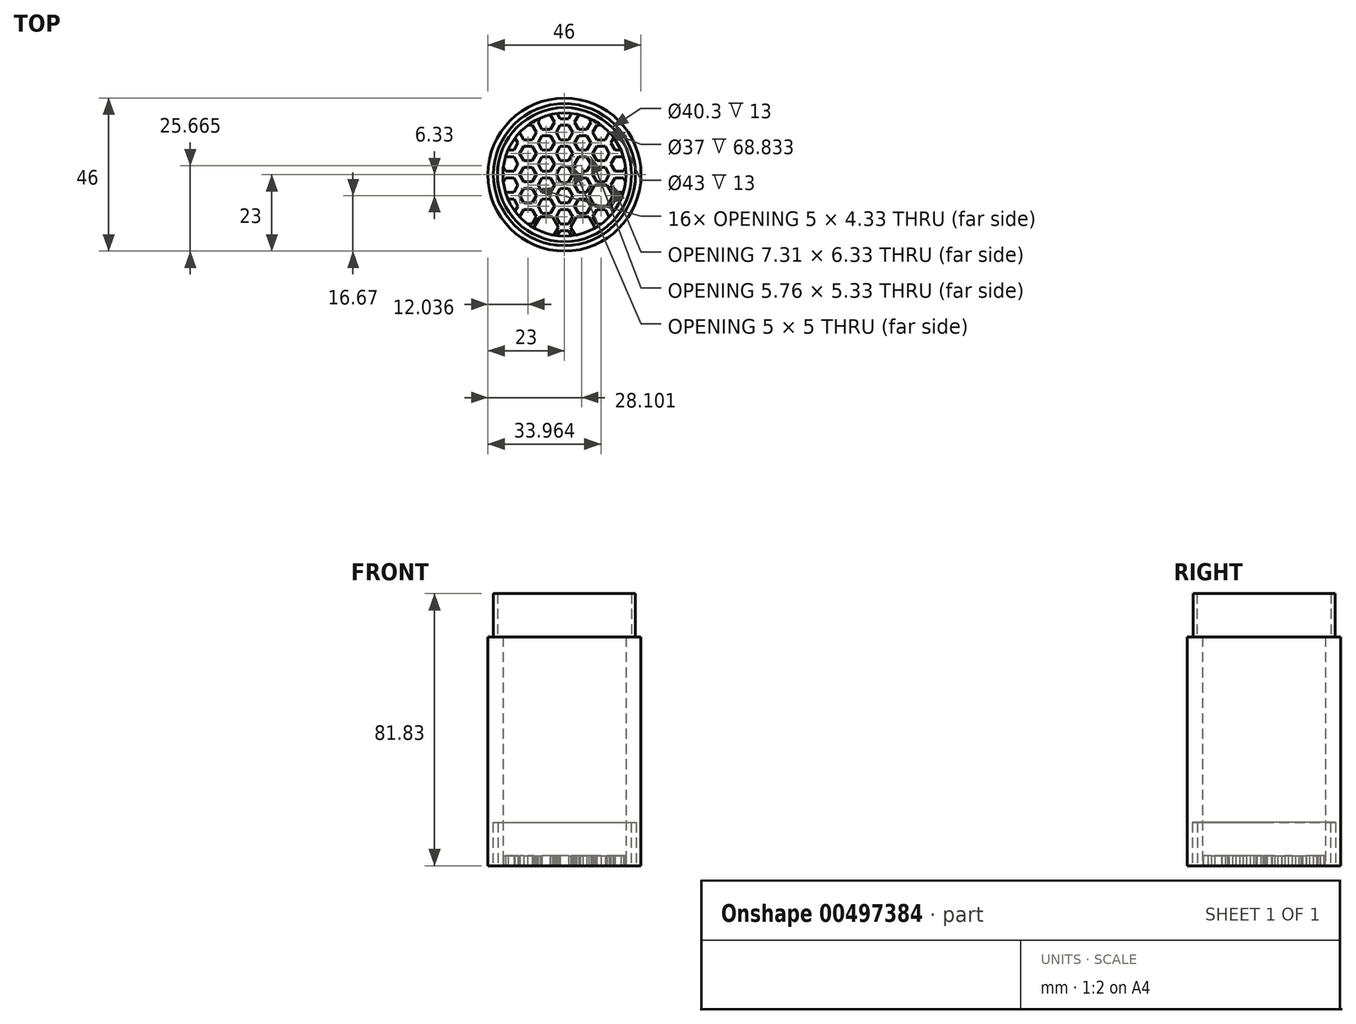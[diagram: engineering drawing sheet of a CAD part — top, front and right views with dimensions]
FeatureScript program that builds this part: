
annotation { "Feature Type Name" : "Feature", "Feature Type Description" : "" }
export const myFeature = defineFeature(function(context is Context, id is Id, definition is map)
    precondition{}
    {
        {
            var Q0;
            Q0=qCreatedBy(makeId("Front.planeOp"),FACE);
            var sketch = newSketch(context, id + "F0", { "sketchPlane" : qUnion([Q0])});
            skLineSegment(sketch, "E0", {"start": v(0, 0) * mm, "end": v(20, 0) * mm});
            skLineSegment(sketch, "E1.bottom", {"start": v(20, 0) * mm, "end": v(18.5, 0) * mm});
            skLineSegment(sketch, "E1.top", {"start": v(20, -13) * mm, "end": v(18.5, -13) * mm});
            skLineSegment(sketch, "E1.left", {"start": v(20, 0) * mm, "end": v(20, -13) * mm});
            skLineSegment(sketch, "E1.right", {"start": v(18.5, 0) * mm, "end": v(18.5, -13) * mm});
            skLineSegment(sketch, "E2.bottom", {"start": v(21.5, 0) * mm, "end": v(20, 0) * mm});
            skLineSegment(sketch, "E2.top", {"start": v(21.5, -13) * mm, "end": v(20, -13) * mm});
            skLineSegment(sketch, "E2.left", {"start": v(21.5, 0) * mm, "end": v(21.5, -13) * mm});
            skLineSegment(sketch, "E3.bottom", {"start": v(23, 0) * mm, "end": v(21.5, 0) * mm});
            skLineSegment(sketch, "E3.top", {"start": v(23, -13) * mm, "end": v(21.5, -13) * mm});
            skLineSegment(sketch, "E3.left", {"start": v(23, 0) * mm, "end": v(23, -13) * mm});
            skLineSegment(sketch, "E4.bottom", {"start": v(23, 0) * mm, "end": v(0, 0) * mm});
            skLineSegment(sketch, "E4.top", {"start": v(23, 55.83) * mm, "end": v(0, 55.83) * mm});
            skLineSegment(sketch, "E4.left", {"start": v(23, 0) * mm, "end": v(23, 55.83) * mm});
            skLineSegment(sketch, "E4.right", {"start": v(0, 0) * mm, "end": v(0, 55.83) * mm});
            skLineSegment(sketch, "E5.bottom", {"start": v(23, 55.83) * mm, "end": v(21.35, 55.83) * mm});
            skLineSegment(sketch, "E5.top", {"start": v(23, 68.83) * mm, "end": v(21.35, 68.83) * mm});
            skLineSegment(sketch, "E5.left", {"start": v(23, 55.83) * mm, "end": v(23, 68.83) * mm});
            skLineSegment(sketch, "E5.right", {"start": v(21.35, 55.83) * mm, "end": v(21.35, 68.83) * mm});
            skLineSegment(sketch, "E6.bottom", {"start": v(21.35, 68.83) * mm, "end": v(20.15, 68.83) * mm});
            skLineSegment(sketch, "E6.top", {"start": v(21.35, 55.83) * mm, "end": v(20.15, 55.83) * mm});
            skLineSegment(sketch, "E6.left", {"start": v(21.35, 68.83) * mm, "end": v(21.35, 55.83) * mm});
            skLineSegment(sketch, "E6.right", {"start": v(20.15, 68.83) * mm, "end": v(20.15, 55.83) * mm});
            skLineSegment(sketch, "E7.bottom", {"start": v(20.15, 68.83) * mm, "end": v(18.5, 68.83) * mm});
            skLineSegment(sketch, "E7.top", {"start": v(20.15, 55.83) * mm, "end": v(18.5, 55.83) * mm});
            skLineSegment(sketch, "E7.right", {"start": v(18.5, 68.83) * mm, "end": v(18.5, 55.83) * mm});
            skLineSegment(sketch, "E8", {"start": v(18.5, 55.83) * mm, "end": v(18.5, 0) * mm});
            skSolve(sketch);
        }
        {
            var Q0;
            {var subQ2=sQuery(id+"F0.wireOp",EDGE,"E5.right");Q0=makeQuery(id+"F0.imprint","IMPRINT",FACE,{"disambiguationData":[TD([[makeQuery(id+"F0.imprint","IMPRINT",EDGE,{"derivedFrom":subQ2}),1.0]])]});}
            var Q1;
            Q1=makeQuery(id+"F0.imprint","IMPRINT",FACE,{"disambiguationData":[TD([[makeQuery(id+"F0.imprint","IMPRINT",EDGE,{"derivedFrom":sQuery(id+"F0.wireOp",EDGE,"E2.left")}),1.0]])]});
            var Q2;
            Q2=makeQuery(id+"F0.imprint","IMPRINT",FACE,{"disambiguationData":[TD([[makeQuery(id+"F0.imprint","IMPRINT",EDGE,{"derivedFrom":sQuery(id+"F0.wireOp",EDGE,"E1.top")}),-1.0]])]});
            var Q3;
            {var subQ3=sQuery(id+"F0.wireOp",EDGE,"E2.bottom");Q3=makeQuery(id+"F0.imprint","IMPRINT",FACE,{"disambiguationData":[TD([[makeQuery(id+"F0.imprint","IMPRINT",EDGE,{"derivedFrom":subQ3}),-1.0]])]});}
            var Q4;
            Q4=sQuery(id+"F0.wireOp",EDGE,"E4.right");
            revolve(context, id + "F1", {"entities" : qUnion([Q0, Q1, Q2, Q3]), "axis" : qUnion([Q4]), "revolveType" : RevolveType.FULL});
        }
        {
            var Q0;
            Q0=makeQuery(id+"F1.opRevolve","SWEPT_FACE",FACE,{"disambiguationData":[OSD([sQuery(id+"F0.wireOp",EDGE,"E1.top")])]});
            var sketch = newSketch(context, id + "F2", { "sketchPlane" : qUnion([Q0])});
            skCircle(sketch, "E9.0", {"center": v(0, 0) * mm, "radius": 20 * mm});
            skCircle(sketch, "E10.0", {"center": v(0, 0) * mm, "radius": 18.5 * mm});
            skCircle(sketch, "E11", {"center": v(0, 0) * mm, "radius": 2.5 * mm});
            skLineSegment(sketch, "E12", {"start": v(-2.5, 0) * mm, "end": v(2.5, 0) * mm});
            skLineSegment(sketch, "E13", {"start": v(0, 2.5) * mm, "end": v(0, -2.5) * mm});
            skArc(sketch, "E14", {"start": v(0, 0) * mm, "mid": v(4.67, 1.25) * mm, "end": v(1.25, -2.17) * mm});
            skArc(sketch, "E15", {"start": v(0, 0) * mm, "mid": v(-4.67, 1.25) * mm, "end": v(-1.25, -2.17) * mm});
            skPoint(sketch, "E16", {"position": v(1.25, -2.17) * mm});
            skPoint(sketch, "E17", {"position": v(1.25, 2.17) * mm});
            skPoint(sketch, "E18", {"position": v(-1.25, 2.17) * mm});
            skPoint(sketch, "E19", {"position": v(-1.25, -2.17) * mm});
            skLineSegment(sketch, "E20", {"start": v(1.25, -2.17) * mm, "end": v(2.5, 0) * mm});
            skLineSegment(sketch, "E21", {"start": v(1.25, 2.17) * mm, "end": v(2.5, 0) * mm});
            skLineSegment(sketch, "E22", {"start": v(1.25, 2.17) * mm, "end": v(-1.25, 2.17) * mm});
            skLineSegment(sketch, "E23", {"start": v(-1.25, 2.17) * mm, "end": v(-2.5, 0) * mm});
            skLineSegment(sketch, "E24", {"start": v(-2.5, 0) * mm, "end": v(-1.25, -2.17) * mm});
            skLineSegment(sketch, "E25", {"start": v(-1.25, -2.17) * mm, "end": v(1.25, -2.17) * mm});
            skLineSegment(sketch, "E26.0", {"start": v(-3.65, 0) * mm, "end": v(-1.83, -3.17) * mm});
            skLineSegment(sketch, "E26.1", {"start": v(1.83, -3.17) * mm, "end": v(3.65, 0) * mm});
            skLineSegment(sketch, "E26.2", {"start": v(1.83, 3.17) * mm, "end": v(3.65, 0) * mm});
            skLineSegment(sketch, "E26.3", {"start": v(-1.83, -3.17) * mm, "end": v(1.83, -3.17) * mm});
            skLineSegment(sketch, "E26.4", {"start": v(1.83, 3.17) * mm, "end": v(-1.83, 3.17) * mm});
            skLineSegment(sketch, "E26.5", {"start": v(-1.83, 3.17) * mm, "end": v(-3.65, 0) * mm});
            skLineSegment(sketch, "E27.MirrorCS", {"start": v(-4.23, -1) * mm, "end": v(-2.98, -3.17) * mm});
            skLineSegment(sketch, "E28.MirrorCS", {"start": v(-2.98, -3.17) * mm, "end": v(-4.23, -5.33) * mm});
            skLineSegment(sketch, "E29.MirrorCS", {"start": v(-4.23, -5.33) * mm, "end": v(-6.73, -5.33) * mm});
            skLineSegment(sketch, "E30.MirrorCS", {"start": v(-6.73, -1) * mm, "end": v(-4.23, -1) * mm});
            skLineSegment(sketch, "E31.MirrorCS", {"start": v(-7.98, -3.17) * mm, "end": v(-6.73, -1) * mm});
            skLineSegment(sketch, "E32.MirrorCS", {"start": v(-7.98, -3.17) * mm, "end": v(-6.73, -5.33) * mm});
            skLineSegment(sketch, "E33.MirrorCS", {"start": v(-1.83, -3.17) * mm, "end": v(-3.65, -6.33) * mm});
            skLineSegment(sketch, "E34.MirrorCS", {"start": v(-7.3, 0) * mm, "end": v(-3.65, 0) * mm});
            skLineSegment(sketch, "E35.MirrorCS", {"start": v(-9.14, -3.17) * mm, "end": v(-7.3, 0) * mm});
            skLineSegment(sketch, "E36.MirrorCS", {"start": v(-3.65, -6.33) * mm, "end": v(-7.3, -6.33) * mm});
            skLineSegment(sketch, "E37.MirrorCS", {"start": v(-9.14, -3.17) * mm, "end": v(-7.3, -6.33) * mm});
            skLineSegment(sketch, "E38.MirrorCS", {"start": v(-7.3, 6.33) * mm, "end": v(-3.65, 6.33) * mm});
            skLineSegment(sketch, "E39.MirrorCS", {"start": v(-9.14, 9.5) * mm, "end": v(-7.3, 6.33) * mm});
            skLineSegment(sketch, "E40.MirrorCS", {"start": v(-7.98, 9.5) * mm, "end": v(-6.73, 7.33) * mm});
            skLineSegment(sketch, "E41.MirrorCS", {"start": v(-6.73, 7.33) * mm, "end": v(-4.23, 7.33) * mm});
            skLineSegment(sketch, "E42.MirrorCS", {"start": v(-3.65, 12.66) * mm, "end": v(-7.3, 12.66) * mm});
            skLineSegment(sketch, "E43.MirrorCS", {"start": v(-4.23, 11.66) * mm, "end": v(-6.73, 11.66) * mm});
            skLineSegment(sketch, "E44.MirrorCS", {"start": v(-7.98, 9.5) * mm, "end": v(-6.73, 11.66) * mm});
            skLineSegment(sketch, "E45.MirrorCS", {"start": v(-9.14, 9.5) * mm, "end": v(-7.3, 12.66) * mm});
            skLineSegment(sketch, "E46.MirrorCS", {"start": v(-2.98, 9.5) * mm, "end": v(-4.23, 11.66) * mm});
            skLineSegment(sketch, "E47.MirrorCS", {"start": v(-1.83, 9.5) * mm, "end": v(-3.65, 12.66) * mm});
            skLineSegment(sketch, "E48.MirrorCS", {"start": v(-4.23, 7.33) * mm, "end": v(-2.98, 9.5) * mm});
            skLineSegment(sketch, "E49.MirrorCS", {"start": v(-3.65, 6.33) * mm, "end": v(-1.83, 9.5) * mm});
            skLineSegment(sketch, "E50.MirrorCS", {"start": v(1.25, 4.17) * mm, "end": v(-1.25, 4.17) * mm});
            skLineSegment(sketch, "E51.MirrorCS", {"start": v(-1.25, 4.17) * mm, "end": v(-2.5, 6.33) * mm});
            skLineSegment(sketch, "E52.MirrorCS", {"start": v(-1.83, 3.17) * mm, "end": v(-3.65, 6.33) * mm});
            skLineSegment(sketch, "E53.MirrorCS", {"start": v(1.83, 3.17) * mm, "end": v(3.65, 6.33) * mm});
            skLineSegment(sketch, "E54.MirrorCS", {"start": v(1.25, 4.17) * mm, "end": v(2.5, 6.33) * mm});
            skLineSegment(sketch, "E55.MirrorCS", {"start": v(1.25, 8.5) * mm, "end": v(2.5, 6.33) * mm});
            skLineSegment(sketch, "E56.MirrorCS", {"start": v(1.83, 9.5) * mm, "end": v(3.65, 6.33) * mm});
            skLineSegment(sketch, "E57.MirrorCS", {"start": v(-1.83, 9.5) * mm, "end": v(1.83, 9.5) * mm});
            skLineSegment(sketch, "E58.MirrorCS", {"start": v(-1.25, 8.5) * mm, "end": v(1.25, 8.5) * mm});
            skLineSegment(sketch, "E59.MirrorCS", {"start": v(-2.5, 6.33) * mm, "end": v(-1.25, 8.5) * mm});
            skLineSegment(sketch, "E60.MirrorCS", {"start": v(-6.73, 1) * mm, "end": v(-4.23, 1) * mm});
            skLineSegment(sketch, "E61.MirrorCS", {"start": v(-7.98, 3.17) * mm, "end": v(-6.73, 1) * mm});
            skLineSegment(sketch, "E62.MirrorCS", {"start": v(-9.14, 3.17) * mm, "end": v(-7.3, 0) * mm});
            skLineSegment(sketch, "E63.MirrorCS", {"start": v(-9.14, 3.17) * mm, "end": v(-7.3, 6.33) * mm});
            skLineSegment(sketch, "E64.MirrorCS", {"start": v(-7.98, 3.17) * mm, "end": v(-6.73, 5.33) * mm});
            skLineSegment(sketch, "E65.MirrorCS", {"start": v(-3.65, 6.33) * mm, "end": v(-7.3, 6.33) * mm});
            skLineSegment(sketch, "E66.MirrorCS", {"start": v(-4.23, 5.33) * mm, "end": v(-6.73, 5.33) * mm});
            skLineSegment(sketch, "E67.MirrorCS", {"start": v(-2.98, 3.17) * mm, "end": v(-4.23, 5.33) * mm});
            skLineSegment(sketch, "E68.MirrorCS", {"start": v(-4.23, 1) * mm, "end": v(-2.98, 3.17) * mm});
            skLineSegment(sketch, "E69.MirrorCS", {"start": v(-1.25, -4.17) * mm, "end": v(1.25, -4.17) * mm});
            skLineSegment(sketch, "E70.MirrorCS", {"start": v(-2.5, -6.33) * mm, "end": v(-1.25, -4.17) * mm});
            skLineSegment(sketch, "E71.MirrorCS", {"start": v(-1.25, -8.5) * mm, "end": v(-2.5, -6.33) * mm});
            skLineSegment(sketch, "E72.MirrorCS", {"start": v(1.25, -8.5) * mm, "end": v(-1.25, -8.5) * mm});
            skLineSegment(sketch, "E73.MirrorCS", {"start": v(1.25, -8.5) * mm, "end": v(2.5, -6.33) * mm});
            skLineSegment(sketch, "E74.MirrorCS", {"start": v(1.25, -4.17) * mm, "end": v(2.5, -6.33) * mm});
            skLineSegment(sketch, "E75.MirrorCS", {"start": v(1.83, -3.17) * mm, "end": v(3.65, -6.33) * mm});
            skLineSegment(sketch, "E76.MirrorCS", {"start": v(1.83, -9.5) * mm, "end": v(3.65, -6.33) * mm});
            skLineSegment(sketch, "E77.MirrorCS", {"start": v(1.83, -9.5) * mm, "end": v(-1.83, -9.5) * mm});
            skLineSegment(sketch, "E78.MirrorCS", {"start": v(-1.83, -9.5) * mm, "end": v(-3.65, -6.33) * mm});
            skLineSegment(sketch, "E79.MirrorCS", {"start": v(-4.23, -7.33) * mm, "end": v(-2.98, -9.5) * mm});
            skLineSegment(sketch, "E80.MirrorCS", {"start": v(-6.73, -7.33) * mm, "end": v(-4.23, -7.33) * mm});
            skLineSegment(sketch, "E81.MirrorCS", {"start": v(-7.98, -9.5) * mm, "end": v(-6.73, -7.33) * mm});
            skLineSegment(sketch, "E82.MirrorCS", {"start": v(-7.98, -9.5) * mm, "end": v(-6.73, -11.66) * mm});
            skLineSegment(sketch, "E83.MirrorCS", {"start": v(-4.23, -11.66) * mm, "end": v(-6.73, -11.66) * mm});
            skLineSegment(sketch, "E84.MirrorCS", {"start": v(-2.98, -9.5) * mm, "end": v(-4.23, -11.66) * mm});
            skLineSegment(sketch, "E85.MirrorCS", {"start": v(-9.14, -9.5) * mm, "end": v(-7.3, -6.33) * mm});
            skLineSegment(sketch, "E86.MirrorCS", {"start": v(-9.14, -9.5) * mm, "end": v(-7.3, -12.66) * mm});
            skLineSegment(sketch, "E87.MirrorCS", {"start": v(-7.3, -12.66) * mm, "end": v(-3.65, -12.66) * mm});
            skLineSegment(sketch, "E88.MirrorCS", {"start": v(-1.83, -9.5) * mm, "end": v(-3.65, -12.66) * mm});
            skLineSegment(sketch, "E89.MirrorCS", {"start": v(1.83, -9.5) * mm, "end": v(3.65, -12.66) * mm});
            skLineSegment(sketch, "E90.MirrorCS", {"start": v(7.3, -12.66) * mm, "end": v(3.65, -12.66) * mm});
            skLineSegment(sketch, "E91.MirrorCS", {"start": v(9.14, -9.5) * mm, "end": v(7.3, -12.66) * mm});
            skLineSegment(sketch, "E92.MirrorCS", {"start": v(9.14, -9.5) * mm, "end": v(7.3, -6.33) * mm});
            skLineSegment(sketch, "E93.MirrorCS", {"start": v(3.65, -6.33) * mm, "end": v(7.3, -6.33) * mm});
            skLineSegment(sketch, "E94.MirrorCS", {"start": v(9.14, -3.17) * mm, "end": v(7.3, -6.33) * mm});
            skLineSegment(sketch, "E95.MirrorCS", {"start": v(9.14, -3.17) * mm, "end": v(7.3, 0) * mm});
            skLineSegment(sketch, "E96.MirrorCS", {"start": v(7.3, 0) * mm, "end": v(3.65, 0) * mm});
            skLineSegment(sketch, "E97.MirrorCS", {"start": v(9.14, 3.17) * mm, "end": v(7.3, 0) * mm});
            skLineSegment(sketch, "E98.MirrorCS", {"start": v(9.14, 3.17) * mm, "end": v(7.3, 6.33) * mm});
            skLineSegment(sketch, "E99.MirrorCS", {"start": v(7.3, 6.33) * mm, "end": v(3.65, 6.33) * mm});
            skLineSegment(sketch, "E100.MirrorCS", {"start": v(7.98, 9.5) * mm, "end": v(6.73, 7.33) * mm});
            skLineSegment(sketch, "E101.MirrorCS", {"start": v(9.14, 9.5) * mm, "end": v(7.3, 12.66) * mm});
            skLineSegment(sketch, "E102.MirrorCS", {"start": v(3.65, 12.66) * mm, "end": v(7.3, 12.66) * mm});
            skLineSegment(sketch, "E103.MirrorCS", {"start": v(1.83, 9.5) * mm, "end": v(3.65, 12.66) * mm});
            skLineSegment(sketch, "E104.MirrorCS", {"start": v(9.14, 9.5) * mm, "end": v(7.3, 6.33) * mm});
            skLineSegment(sketch, "E105.MirrorCS", {"start": v(7.98, 9.5) * mm, "end": v(6.73, 11.66) * mm});
            skLineSegment(sketch, "E106.MirrorCS", {"start": v(4.23, 11.66) * mm, "end": v(6.73, 11.66) * mm});
            skLineSegment(sketch, "E107.MirrorCS", {"start": v(2.98, 9.5) * mm, "end": v(4.23, 11.66) * mm});
            skLineSegment(sketch, "E108.MirrorCS", {"start": v(4.23, 7.33) * mm, "end": v(2.98, 9.5) * mm});
            skLineSegment(sketch, "E109.MirrorCS", {"start": v(6.73, 7.33) * mm, "end": v(4.23, 7.33) * mm});
            skLineSegment(sketch, "E110.MirrorCS", {"start": v(4.23, 5.33) * mm, "end": v(6.73, 5.33) * mm});
            skLineSegment(sketch, "E111.MirrorCS", {"start": v(7.98, 3.17) * mm, "end": v(6.73, 5.33) * mm});
            skLineSegment(sketch, "E112.MirrorCS", {"start": v(2.98, 3.17) * mm, "end": v(4.23, 5.33) * mm});
            skLineSegment(sketch, "E113.MirrorCS", {"start": v(7.98, 3.17) * mm, "end": v(6.73, 1) * mm});
            skLineSegment(sketch, "E114.MirrorCS", {"start": v(6.73, 1) * mm, "end": v(4.23, 1) * mm});
            skLineSegment(sketch, "E115.MirrorCS", {"start": v(4.23, 1) * mm, "end": v(2.98, 3.17) * mm});
            skLineSegment(sketch, "E116.MirrorCS", {"start": v(2.98, -3.17) * mm, "end": v(4.23, -5.33) * mm});
            skLineSegment(sketch, "E117.MirrorCS", {"start": v(4.23, -5.33) * mm, "end": v(6.73, -5.33) * mm});
            skLineSegment(sketch, "E118.MirrorCS", {"start": v(7.98, -3.17) * mm, "end": v(6.73, -5.33) * mm});
            skLineSegment(sketch, "E119.MirrorCS", {"start": v(7.98, -3.17) * mm, "end": v(6.73, -1) * mm});
            skLineSegment(sketch, "E120.MirrorCS", {"start": v(6.73, -1) * mm, "end": v(4.23, -1) * mm});
            skLineSegment(sketch, "E121.MirrorCS", {"start": v(4.23, -1) * mm, "end": v(2.98, -3.17) * mm});
            skLineSegment(sketch, "E122.MirrorCS", {"start": v(4.23, -7.33) * mm, "end": v(2.98, -9.5) * mm});
            skLineSegment(sketch, "E123.MirrorCS", {"start": v(6.73, -7.33) * mm, "end": v(4.23, -7.33) * mm});
            skLineSegment(sketch, "E124.MirrorCS", {"start": v(7.98, -9.5) * mm, "end": v(6.73, -7.33) * mm});
            skLineSegment(sketch, "E125.MirrorCS", {"start": v(7.98, -9.5) * mm, "end": v(6.73, -11.66) * mm});
            skLineSegment(sketch, "E126.MirrorCS", {"start": v(4.23, -11.66) * mm, "end": v(6.73, -11.66) * mm});
            skLineSegment(sketch, "E127.MirrorCS", {"start": v(2.98, -9.5) * mm, "end": v(4.23, -11.66) * mm});
            skLineSegment(sketch, "E128", {"start": v(5.48, 1) * mm, "end": v(5.48, -1) * mm});
            skLineSegment(sketch, "E129.MirrorCS", {"start": v(12.8, 9.5) * mm, "end": v(9.14, 9.5) * mm});
            skLineSegment(sketch, "E130.MirrorCS", {"start": v(9.14, 3.17) * mm, "end": v(12.8, 3.17) * mm});
            skLineSegment(sketch, "E131.MirrorCS", {"start": v(12.8, -3.17) * mm, "end": v(9.14, -3.17) * mm});
            skLineSegment(sketch, "E132.MirrorCS", {"start": v(9.14, -9.5) * mm, "end": v(12.8, -9.5) * mm});
            skLineSegment(sketch, "E133.MirrorCS", {"start": v(14.62, 0) * mm, "end": v(12.8, -3.17) * mm});
            skLineSegment(sketch, "E134.MirrorCS", {"start": v(12.8, 3.17) * mm, "end": v(14.62, 0) * mm});
            skLineSegment(sketch, "E135.MirrorCS", {"start": v(12.8, 3.17) * mm, "end": v(14.62, 6.33) * mm});
            skLineSegment(sketch, "E136.MirrorCS", {"start": v(14.62, 6.33) * mm, "end": v(12.8, 9.5) * mm});
            skLineSegment(sketch, "E137.MirrorCS", {"start": v(12.8, -3.17) * mm, "end": v(14.62, -6.33) * mm});
            skLineSegment(sketch, "E138.MirrorCS", {"start": v(12.8, -9.5) * mm, "end": v(14.62, -6.33) * mm});
            skLineSegment(sketch, "E139.MirrorCS", {"start": v(9.71, -4.17) * mm, "end": v(8.46, -6.33) * mm});
            skLineSegment(sketch, "E140.MirrorCS", {"start": v(9.71, -8.5) * mm, "end": v(8.46, -6.33) * mm});
            skLineSegment(sketch, "E141.MirrorCS", {"start": v(9.71, -8.5) * mm, "end": v(12.21, -8.5) * mm});
            skLineSegment(sketch, "E142.MirrorCS", {"start": v(12.21, -8.5) * mm, "end": v(13.46, -6.33) * mm});
            skLineSegment(sketch, "E143.MirrorCS", {"start": v(13.46, -6.33) * mm, "end": v(12.21, -4.17) * mm});
            skLineSegment(sketch, "E144.MirrorCS", {"start": v(12.21, -4.17) * mm, "end": v(9.71, -4.17) * mm});
            skLineSegment(sketch, "E145.MirrorCS", {"start": v(9.71, 4.17) * mm, "end": v(12.21, 4.17) * mm});
            skLineSegment(sketch, "E146.MirrorCS", {"start": v(9.71, 4.17) * mm, "end": v(8.46, 6.33) * mm});
            skLineSegment(sketch, "E147.MirrorCS", {"start": v(9.71, 8.5) * mm, "end": v(8.46, 6.33) * mm});
            skLineSegment(sketch, "E148.MirrorCS", {"start": v(12.21, 8.5) * mm, "end": v(9.71, 8.5) * mm});
            skLineSegment(sketch, "E149.MirrorCS", {"start": v(12.21, 4.17) * mm, "end": v(13.46, 6.33) * mm});
            skLineSegment(sketch, "E150.MirrorCS", {"start": v(13.46, 6.33) * mm, "end": v(12.21, 8.5) * mm});
            skLineSegment(sketch, "E151.MirrorCS", {"start": v(9.71, 2.17) * mm, "end": v(12.21, 2.17) * mm});
            skLineSegment(sketch, "E152.MirrorCS", {"start": v(12.21, 2.17) * mm, "end": v(13.46, 0) * mm});
            skLineSegment(sketch, "E153.MirrorCS", {"start": v(13.46, 0) * mm, "end": v(12.21, -2.17) * mm});
            skLineSegment(sketch, "E154.MirrorCS", {"start": v(12.21, -2.17) * mm, "end": v(9.71, -2.17) * mm});
            skLineSegment(sketch, "E155.MirrorCS", {"start": v(9.71, -2.17) * mm, "end": v(8.46, 0) * mm});
            skLineSegment(sketch, "E156.MirrorCS", {"start": v(9.71, 2.17) * mm, "end": v(8.46, 0) * mm});
            skLineSegment(sketch, "E157.MirrorCS", {"start": v(-9.14, -9.5) * mm, "end": v(-12.8, -9.5) * mm});
            skLineSegment(sketch, "E158.MirrorCS", {"start": v(-12.8, -9.5) * mm, "end": v(-14.62, -6.33) * mm});
            skLineSegment(sketch, "E159.MirrorCS", {"start": v(-12.8, -3.17) * mm, "end": v(-14.62, -6.33) * mm});
            skLineSegment(sketch, "E160.MirrorCS", {"start": v(-12.8, -3.17) * mm, "end": v(-9.14, -3.17) * mm});
            skLineSegment(sketch, "E161.MirrorCS", {"start": v(-14.62, 0) * mm, "end": v(-12.8, -3.17) * mm});
            skLineSegment(sketch, "E162.MirrorCS", {"start": v(-12.8, 3.17) * mm, "end": v(-14.62, 0) * mm});
            skLineSegment(sketch, "E163.MirrorCS", {"start": v(-9.14, 3.17) * mm, "end": v(-12.8, 3.17) * mm});
            skLineSegment(sketch, "E164.MirrorCS", {"start": v(-12.8, 3.17) * mm, "end": v(-14.62, 6.33) * mm});
            skLineSegment(sketch, "E165.MirrorCS", {"start": v(-14.62, 6.33) * mm, "end": v(-12.8, 9.5) * mm});
            skLineSegment(sketch, "E166.MirrorCS", {"start": v(-12.8, 9.5) * mm, "end": v(-9.14, 9.5) * mm});
            skLineSegment(sketch, "E167.MirrorCS", {"start": v(-12.21, 8.5) * mm, "end": v(-9.71, 8.5) * mm});
            skLineSegment(sketch, "E168.MirrorCS", {"start": v(-13.46, 6.33) * mm, "end": v(-12.21, 8.5) * mm});
            skLineSegment(sketch, "E169.MirrorCS", {"start": v(-9.71, 8.5) * mm, "end": v(-8.46, 6.33) * mm});
            skLineSegment(sketch, "E170.MirrorCS", {"start": v(-9.71, 4.17) * mm, "end": v(-12.21, 4.17) * mm});
            skLineSegment(sketch, "E171.MirrorCS", {"start": v(-12.21, 4.17) * mm, "end": v(-13.46, 6.33) * mm});
            skLineSegment(sketch, "E172.MirrorCS", {"start": v(-9.71, 4.17) * mm, "end": v(-8.46, 6.33) * mm});
            skLineSegment(sketch, "E173.MirrorCS", {"start": v(-9.71, 2.17) * mm, "end": v(-12.21, 2.17) * mm});
            skLineSegment(sketch, "E174.MirrorCS", {"start": v(-9.71, 2.17) * mm, "end": v(-8.46, 0) * mm});
            skLineSegment(sketch, "E175.MirrorCS", {"start": v(-12.21, 2.17) * mm, "end": v(-13.46, 0) * mm});
            skLineSegment(sketch, "E176.MirrorCS", {"start": v(-9.71, -2.17) * mm, "end": v(-8.46, 0) * mm});
            skLineSegment(sketch, "E177.MirrorCS", {"start": v(-12.21, -2.17) * mm, "end": v(-9.71, -2.17) * mm});
            skLineSegment(sketch, "E178.MirrorCS", {"start": v(-13.46, 0) * mm, "end": v(-12.21, -2.17) * mm});
            skLineSegment(sketch, "E179.MirrorCS", {"start": v(-12.21, -4.17) * mm, "end": v(-9.71, -4.17) * mm});
            skLineSegment(sketch, "E180.MirrorCS", {"start": v(-9.71, -4.17) * mm, "end": v(-8.46, -6.33) * mm});
            skLineSegment(sketch, "E181.MirrorCS", {"start": v(-9.71, -8.5) * mm, "end": v(-8.46, -6.33) * mm});
            skLineSegment(sketch, "E182.MirrorCS", {"start": v(-9.71, -8.5) * mm, "end": v(-12.21, -8.5) * mm});
            skLineSegment(sketch, "E183.MirrorCS", {"start": v(-13.46, -6.33) * mm, "end": v(-12.21, -4.17) * mm});
            skLineSegment(sketch, "E184.MirrorCS", {"start": v(-12.21, -8.5) * mm, "end": v(-13.46, -6.33) * mm});
            skLineSegment(sketch, "E185.MirrorCS", {"start": v(1.25, -10.5) * mm, "end": v(-1.25, -10.5) * mm});
            skLineSegment(sketch, "E186.MirrorCS", {"start": v(-1.25, -10.5) * mm, "end": v(-2.5, -12.66) * mm});
            skLineSegment(sketch, "E187.MirrorCS", {"start": v(1.25, -10.5) * mm, "end": v(2.5, -12.66) * mm});
            skLineSegment(sketch, "E188.MirrorCS", {"start": v(1.25, -14.83) * mm, "end": v(2.5, -12.66) * mm});
            skLineSegment(sketch, "E189.MirrorCS", {"start": v(-1.25, -14.83) * mm, "end": v(1.25, -14.83) * mm});
            skLineSegment(sketch, "E190.MirrorCS", {"start": v(-2.5, -12.66) * mm, "end": v(-1.25, -14.83) * mm});
            skLineSegment(sketch, "E191.MirrorCS", {"start": v(1.83, -15.83) * mm, "end": v(3.65, -12.66) * mm});
            skLineSegment(sketch, "E192.MirrorCS", {"start": v(-1.83, -15.83) * mm, "end": v(-3.65, -12.66) * mm});
            skLineSegment(sketch, "E193.MirrorCS", {"start": v(-1.83, -15.83) * mm, "end": v(1.83, -15.83) * mm});
            skLineSegment(sketch, "E194.MirrorCS", {"start": v(1.25, 10.5) * mm, "end": v(-1.25, 10.5) * mm});
            skLineSegment(sketch, "E195.MirrorCS", {"start": v(-1.25, 10.5) * mm, "end": v(-2.5, 12.66) * mm});
            skLineSegment(sketch, "E196.MirrorCS", {"start": v(1.25, 14.83) * mm, "end": v(2.5, 12.66) * mm});
            skLineSegment(sketch, "E197.MirrorCS", {"start": v(-1.25, 14.83) * mm, "end": v(1.25, 14.83) * mm});
            skLineSegment(sketch, "E198.MirrorCS", {"start": v(1.25, 10.5) * mm, "end": v(2.5, 12.66) * mm});
            skLineSegment(sketch, "E199.MirrorCS", {"start": v(-1.83, 15.83) * mm, "end": v(-3.65, 12.66) * mm});
            skLineSegment(sketch, "E200.MirrorCS", {"start": v(1.83, 15.83) * mm, "end": v(3.65, 12.66) * mm});
            skLineSegment(sketch, "E201.MirrorCS", {"start": v(-2.5, 12.66) * mm, "end": v(-1.25, 14.83) * mm});
            skLineSegment(sketch, "E202.MirrorCS", {"start": v(-1.83, 15.83) * mm, "end": v(1.83, 15.83) * mm});
            skLineSegment(sketch, "E203.MirrorCS", {"start": v(5.48, -1) * mm, "end": v(5.48, 1) * mm});
            skLineSegment(sketch, "E204.MirrorCS", {"start": v(15.2, -5.33) * mm, "end": v(17.7, -5.33) * mm});
            skLineSegment(sketch, "E205.MirrorCS", {"start": v(18.95, -3.17) * mm, "end": v(17.7, -5.33) * mm});
            skLineSegment(sketch, "E206.MirrorCS", {"start": v(18.95, -3.17) * mm, "end": v(17.7, -1) * mm});
            skLineSegment(sketch, "E207.MirrorCS", {"start": v(17.7, -1) * mm, "end": v(15.2, -1) * mm});
            skLineSegment(sketch, "E208.MirrorCS", {"start": v(15.2, -1) * mm, "end": v(13.95, -3.17) * mm});
            skLineSegment(sketch, "E209.MirrorCS", {"start": v(13.95, -3.17) * mm, "end": v(15.2, -5.33) * mm});
            skLineSegment(sketch, "E210.MirrorCS", {"start": v(17.7, 1) * mm, "end": v(15.2, 1) * mm});
            skLineSegment(sketch, "E211.MirrorCS", {"start": v(18.95, 3.17) * mm, "end": v(17.7, 1) * mm});
            skLineSegment(sketch, "E212.MirrorCS", {"start": v(18.95, 3.17) * mm, "end": v(17.7, 5.33) * mm});
            skLineSegment(sketch, "E213.MirrorCS", {"start": v(15.2, 5.33) * mm, "end": v(17.7, 5.33) * mm});
            skLineSegment(sketch, "E214.MirrorCS", {"start": v(13.95, 3.17) * mm, "end": v(15.2, 5.33) * mm});
            skLineSegment(sketch, "E215.MirrorCS", {"start": v(15.2, 1) * mm, "end": v(13.95, 3.17) * mm});
            skLineSegment(sketch, "E216.MirrorCS", {"start": v(18.27, 0) * mm, "end": v(14.62, 0) * mm});
            skLineSegment(sketch, "E217.MirrorCS", {"start": v(20.1, -3.17) * mm, "end": v(18.27, 0) * mm});
            skLineSegment(sketch, "E218.MirrorCS", {"start": v(20.1, -3.17) * mm, "end": v(18.27, -6.33) * mm});
            skLineSegment(sketch, "E219.MirrorCS", {"start": v(14.62, -6.33) * mm, "end": v(18.27, -6.33) * mm});
            skLineSegment(sketch, "E220.MirrorCS", {"start": v(20.1, 3.17) * mm, "end": v(18.27, 0) * mm});
            skLineSegment(sketch, "E221.MirrorCS", {"start": v(20.1, 3.17) * mm, "end": v(18.27, 6.33) * mm});
            skLineSegment(sketch, "E222.MirrorCS", {"start": v(18.27, 6.33) * mm, "end": v(14.62, 6.33) * mm});
            skLineSegment(sketch, "E223.MirrorCS", {"start": v(17.7, 7.33) * mm, "end": v(15.2, 7.33) * mm});
            skLineSegment(sketch, "E224.MirrorCS", {"start": v(18.95, 9.5) * mm, "end": v(17.7, 7.33) * mm});
            skLineSegment(sketch, "E225.MirrorCS", {"start": v(18.95, 9.5) * mm, "end": v(17.7, 11.66) * mm});
            skLineSegment(sketch, "E226.MirrorCS", {"start": v(15.2, 11.66) * mm, "end": v(17.7, 11.66) * mm});
            skLineSegment(sketch, "E227.MirrorCS", {"start": v(13.95, 9.5) * mm, "end": v(15.2, 11.66) * mm});
            skLineSegment(sketch, "E228.MirrorCS", {"start": v(15.2, 7.33) * mm, "end": v(13.95, 9.5) * mm});
            skLineSegment(sketch, "E229.MirrorCS", {"start": v(20.1, 9.5) * mm, "end": v(18.27, 6.33) * mm});
            skLineSegment(sketch, "E230.MirrorCS", {"start": v(20.1, 9.5) * mm, "end": v(18.27, 12.66) * mm});
            skLineSegment(sketch, "E231.MirrorCS", {"start": v(14.62, 12.66) * mm, "end": v(18.27, 12.66) * mm});
            skLineSegment(sketch, "E232.MirrorCS", {"start": v(17.7, -7.33) * mm, "end": v(15.2, -7.33) * mm});
            skLineSegment(sketch, "E233.MirrorCS", {"start": v(15.2, -7.33) * mm, "end": v(13.95, -9.5) * mm});
            skLineSegment(sketch, "E234.MirrorCS", {"start": v(13.95, -9.5) * mm, "end": v(15.2, -11.66) * mm});
            skLineSegment(sketch, "E235.MirrorCS", {"start": v(15.2, -11.66) * mm, "end": v(17.7, -11.66) * mm});
            skLineSegment(sketch, "E236.MirrorCS", {"start": v(18.95, -9.5) * mm, "end": v(17.7, -11.66) * mm});
            skLineSegment(sketch, "E237.MirrorCS", {"start": v(18.95, -9.5) * mm, "end": v(17.7, -7.33) * mm});
            skLineSegment(sketch, "E238.MirrorCS", {"start": v(20.1, -9.5) * mm, "end": v(18.27, -6.33) * mm});
            skLineSegment(sketch, "E239.MirrorCS", {"start": v(20.1, -9.5) * mm, "end": v(18.27, -12.66) * mm});
            skLineSegment(sketch, "E240.MirrorCS", {"start": v(18.27, -12.66) * mm, "end": v(14.62, -12.66) * mm});
            skLineSegment(sketch, "E241.MirrorCS", {"start": v(12.8, 9.5) * mm, "end": v(14.62, 12.66) * mm});
            skLineSegment(sketch, "E242.MirrorCS", {"start": v(12.8, -9.5) * mm, "end": v(14.62, -12.66) * mm});
            skLineSegment(sketch, "E243.MirrorCS", {"start": v(-18.27, -12.66) * mm, "end": v(-14.62, -12.66) * mm});
            skLineSegment(sketch, "E244.MirrorCS", {"start": v(-20.1, -9.5) * mm, "end": v(-18.27, -12.66) * mm});
            skLineSegment(sketch, "E245.MirrorCS", {"start": v(-20.1, -9.5) * mm, "end": v(-18.27, -6.33) * mm});
            skLineSegment(sketch, "E246.MirrorCS", {"start": v(-14.62, -6.33) * mm, "end": v(-18.27, -6.33) * mm});
            skLineSegment(sketch, "E247.MirrorCS", {"start": v(-20.1, -3.17) * mm, "end": v(-18.27, -6.33) * mm});
            skLineSegment(sketch, "E248.MirrorCS", {"start": v(-20.1, -3.17) * mm, "end": v(-18.27, 0) * mm});
            skLineSegment(sketch, "E249.MirrorCS", {"start": v(-18.27, 0) * mm, "end": v(-14.62, 0) * mm});
            skLineSegment(sketch, "E250.MirrorCS", {"start": v(-20.1, 3.17) * mm, "end": v(-18.27, 0) * mm});
            skLineSegment(sketch, "E251.MirrorCS", {"start": v(-20.1, 3.17) * mm, "end": v(-18.27, 6.33) * mm});
            skLineSegment(sketch, "E252.MirrorCS", {"start": v(-18.27, 6.33) * mm, "end": v(-14.62, 6.33) * mm});
            skLineSegment(sketch, "E253.MirrorCS", {"start": v(-20.1, 9.5) * mm, "end": v(-18.27, 6.33) * mm});
            skLineSegment(sketch, "E254.MirrorCS", {"start": v(-20.1, 9.5) * mm, "end": v(-18.27, 12.66) * mm});
            skLineSegment(sketch, "E255.MirrorCS", {"start": v(-14.62, 12.66) * mm, "end": v(-18.27, 12.66) * mm});
            skLineSegment(sketch, "E256.MirrorCS", {"start": v(-12.8, 9.5) * mm, "end": v(-14.62, 12.66) * mm});
            skLineSegment(sketch, "E257.MirrorCS", {"start": v(-15.2, -11.66) * mm, "end": v(-17.7, -11.66) * mm});
            skLineSegment(sketch, "E258.MirrorCS", {"start": v(-13.95, -9.5) * mm, "end": v(-15.2, -11.66) * mm});
            skLineSegment(sketch, "E259.MirrorCS", {"start": v(-15.2, -7.33) * mm, "end": v(-13.95, -9.5) * mm});
            skLineSegment(sketch, "E260.MirrorCS", {"start": v(-17.7, -7.33) * mm, "end": v(-15.2, -7.33) * mm});
            skLineSegment(sketch, "E261.MirrorCS", {"start": v(-18.95, -9.5) * mm, "end": v(-17.7, -7.33) * mm});
            skLineSegment(sketch, "E262.MirrorCS", {"start": v(-18.95, -9.5) * mm, "end": v(-17.7, -11.66) * mm});
            skLineSegment(sketch, "E263.MirrorCS", {"start": v(-15.2, -5.33) * mm, "end": v(-17.7, -5.33) * mm});
            skLineSegment(sketch, "E264.MirrorCS", {"start": v(-13.95, -3.17) * mm, "end": v(-15.2, -5.33) * mm});
            skLineSegment(sketch, "E265.MirrorCS", {"start": v(-15.2, -1) * mm, "end": v(-13.95, -3.17) * mm});
            skLineSegment(sketch, "E266.MirrorCS", {"start": v(-17.7, -1) * mm, "end": v(-15.2, -1) * mm});
            skLineSegment(sketch, "E267.MirrorCS", {"start": v(-18.95, -3.17) * mm, "end": v(-17.7, -1) * mm});
            skLineSegment(sketch, "E268.MirrorCS", {"start": v(-18.95, -3.17) * mm, "end": v(-17.7, -5.33) * mm});
            skLineSegment(sketch, "E269.MirrorCS", {"start": v(-17.7, 1) * mm, "end": v(-15.2, 1) * mm});
            skLineSegment(sketch, "E270.MirrorCS", {"start": v(-15.2, 1) * mm, "end": v(-13.95, 3.17) * mm});
            skLineSegment(sketch, "E271.MirrorCS", {"start": v(-13.95, 3.17) * mm, "end": v(-15.2, 5.33) * mm});
            skLineSegment(sketch, "E272.MirrorCS", {"start": v(-15.2, 5.33) * mm, "end": v(-17.7, 5.33) * mm});
            skLineSegment(sketch, "E273.MirrorCS", {"start": v(-18.95, 3.17) * mm, "end": v(-17.7, 5.33) * mm});
            skLineSegment(sketch, "E274.MirrorCS", {"start": v(-18.95, 3.17) * mm, "end": v(-17.7, 1) * mm});
            skLineSegment(sketch, "E275.MirrorCS", {"start": v(-17.7, 7.33) * mm, "end": v(-15.2, 7.33) * mm});
            skLineSegment(sketch, "E276.MirrorCS", {"start": v(-15.2, 7.33) * mm, "end": v(-13.95, 9.5) * mm});
            skLineSegment(sketch, "E277.MirrorCS", {"start": v(-13.95, 9.5) * mm, "end": v(-15.2, 11.66) * mm});
            skLineSegment(sketch, "E278.MirrorCS", {"start": v(-15.2, 11.66) * mm, "end": v(-17.7, 11.66) * mm});
            skLineSegment(sketch, "E279.MirrorCS", {"start": v(-18.95, 9.5) * mm, "end": v(-17.7, 11.66) * mm});
            skLineSegment(sketch, "E280.MirrorCS", {"start": v(-18.95, 9.5) * mm, "end": v(-17.7, 7.33) * mm});
            skLineSegment(sketch, "E281.MirrorCS", {"start": v(-12.8, -9.5) * mm, "end": v(-14.62, -12.66) * mm});
            skLineSegment(sketch, "E282.MirrorCS", {"start": v(1.83, 15.83) * mm, "end": v(3.65, 19) * mm});
            skLineSegment(sketch, "E283.MirrorCS", {"start": v(-1.83, 15.83) * mm, "end": v(-3.65, 19) * mm});
            skLineSegment(sketch, "E284.MirrorCS", {"start": v(-1.83, 22.16) * mm, "end": v(-3.65, 19) * mm});
            skLineSegment(sketch, "E285.MirrorCS", {"start": v(-1.83, 22.16) * mm, "end": v(1.83, 22.16) * mm});
            skLineSegment(sketch, "E286.MirrorCS", {"start": v(1.83, 22.16) * mm, "end": v(3.65, 19) * mm});
            skLineSegment(sketch, "E287.MirrorCS", {"start": v(1.25, 21.16) * mm, "end": v(2.5, 19) * mm});
            skLineSegment(sketch, "E288.MirrorCS", {"start": v(1.25, 21.16) * mm, "end": v(-1.25, 21.16) * mm});
            skLineSegment(sketch, "E289.MirrorCS", {"start": v(-1.25, 21.16) * mm, "end": v(-2.5, 19) * mm});
            skLineSegment(sketch, "E290.MirrorCS", {"start": v(-2.5, 19) * mm, "end": v(-1.25, 16.83) * mm});
            skLineSegment(sketch, "E291.MirrorCS", {"start": v(-1.25, 16.83) * mm, "end": v(1.25, 16.83) * mm});
            skLineSegment(sketch, "E292.MirrorCS", {"start": v(1.25, 16.83) * mm, "end": v(2.5, 19) * mm});
            skLineSegment(sketch, "E293.MirrorCS", {"start": v(7.3, 12.66) * mm, "end": v(3.65, 12.66) * mm});
            skLineSegment(sketch, "E294.MirrorCS", {"start": v(7.3, 19) * mm, "end": v(3.65, 19) * mm});
            skLineSegment(sketch, "E295.MirrorCS", {"start": v(9.14, 15.83) * mm, "end": v(7.3, 19) * mm});
            skLineSegment(sketch, "E296.MirrorCS", {"start": v(9.14, 15.83) * mm, "end": v(7.3, 12.66) * mm});
            skLineSegment(sketch, "E297.MirrorCS", {"start": v(7.98, 15.83) * mm, "end": v(6.73, 18) * mm});
            skLineSegment(sketch, "E298.MirrorCS", {"start": v(6.73, 18) * mm, "end": v(4.23, 18) * mm});
            skLineSegment(sketch, "E299.MirrorCS", {"start": v(4.23, 18) * mm, "end": v(2.98, 15.83) * mm});
            skLineSegment(sketch, "E300.MirrorCS", {"start": v(2.98, 15.83) * mm, "end": v(4.23, 13.66) * mm});
            skLineSegment(sketch, "E301.MirrorCS", {"start": v(4.23, 13.66) * mm, "end": v(6.73, 13.66) * mm});
            skLineSegment(sketch, "E302.MirrorCS", {"start": v(7.98, 15.83) * mm, "end": v(6.73, 13.66) * mm});
            skLineSegment(sketch, "E303.MirrorCS", {"start": v(9.14, 15.83) * mm, "end": v(12.8, 15.83) * mm});
            skLineSegment(sketch, "E304.MirrorCS", {"start": v(12.8, 15.83) * mm, "end": v(14.62, 12.66) * mm});
            skLineSegment(sketch, "E305.MirrorCS", {"start": v(14.62, 12.66) * mm, "end": v(12.8, 9.5) * mm});
            skLineSegment(sketch, "E306.MirrorCS", {"start": v(12.21, 14.83) * mm, "end": v(13.46, 12.66) * mm});
            skLineSegment(sketch, "E307.MirrorCS", {"start": v(9.71, 14.83) * mm, "end": v(12.21, 14.83) * mm});
            skLineSegment(sketch, "E308.MirrorCS", {"start": v(9.71, 14.83) * mm, "end": v(8.46, 12.66) * mm});
            skLineSegment(sketch, "E309.MirrorCS", {"start": v(9.71, 10.5) * mm, "end": v(8.46, 12.66) * mm});
            skLineSegment(sketch, "E310.MirrorCS", {"start": v(12.21, 10.5) * mm, "end": v(9.71, 10.5) * mm});
            skLineSegment(sketch, "E311.MirrorCS", {"start": v(13.46, 12.66) * mm, "end": v(12.21, 10.5) * mm});
            skLineSegment(sketch, "E312.MirrorCS", {"start": v(-7.3, 12.66) * mm, "end": v(-3.65, 12.66) * mm});
            skLineSegment(sketch, "E313.MirrorCS", {"start": v(-7.3, 19) * mm, "end": v(-3.65, 19) * mm});
            skLineSegment(sketch, "E314.MirrorCS", {"start": v(-9.14, 15.83) * mm, "end": v(-7.3, 19) * mm});
            skLineSegment(sketch, "E315.MirrorCS", {"start": v(-9.14, 15.83) * mm, "end": v(-7.3, 12.66) * mm});
            skLineSegment(sketch, "E316.MirrorCS", {"start": v(-4.23, 13.66) * mm, "end": v(-6.73, 13.66) * mm});
            skLineSegment(sketch, "E317.MirrorCS", {"start": v(-7.98, 15.83) * mm, "end": v(-6.73, 13.66) * mm});
            skLineSegment(sketch, "E318.MirrorCS", {"start": v(-2.98, 15.83) * mm, "end": v(-4.23, 13.66) * mm});
            skLineSegment(sketch, "E319.MirrorCS", {"start": v(-7.98, 15.83) * mm, "end": v(-6.73, 18) * mm});
            skLineSegment(sketch, "E320.MirrorCS", {"start": v(-6.73, 18) * mm, "end": v(-4.23, 18) * mm});
            skLineSegment(sketch, "E321.MirrorCS", {"start": v(-4.23, 18) * mm, "end": v(-2.98, 15.83) * mm});
            skLineSegment(sketch, "E322.MirrorCS", {"start": v(-12.21, 10.5) * mm, "end": v(-9.71, 10.5) * mm});
            skLineSegment(sketch, "E323.MirrorCS", {"start": v(-9.71, 10.5) * mm, "end": v(-8.46, 12.66) * mm});
            skLineSegment(sketch, "E324.MirrorCS", {"start": v(-9.71, 14.83) * mm, "end": v(-8.46, 12.66) * mm});
            skLineSegment(sketch, "E325.MirrorCS", {"start": v(-13.46, 12.66) * mm, "end": v(-12.21, 10.5) * mm});
            skLineSegment(sketch, "E326.MirrorCS", {"start": v(-12.21, 14.83) * mm, "end": v(-13.46, 12.66) * mm});
            skLineSegment(sketch, "E327.MirrorCS", {"start": v(-9.71, 14.83) * mm, "end": v(-12.21, 14.83) * mm});
            skLineSegment(sketch, "E328.MirrorCS", {"start": v(-12.8, 15.83) * mm, "end": v(-14.62, 12.66) * mm});
            skLineSegment(sketch, "E329.MirrorCS", {"start": v(-9.14, 15.83) * mm, "end": v(-12.8, 15.83) * mm});
            skLineSegment(sketch, "E330.MirrorCS", {"start": v(-9.14, 22.16) * mm, "end": v(-7.3, 19) * mm});
            skLineSegment(sketch, "E331.MirrorCS", {"start": v(-12.8, 22.16) * mm, "end": v(-9.14, 22.16) * mm});
            skLineSegment(sketch, "E332.MirrorCS", {"start": v(-14.62, 19) * mm, "end": v(-12.8, 22.16) * mm});
            skLineSegment(sketch, "E333.MirrorCS", {"start": v(-12.8, 15.83) * mm, "end": v(-14.62, 19) * mm});
            skLineSegment(sketch, "E334.MirrorCS", {"start": v(-9.71, 16.83) * mm, "end": v(-8.46, 19) * mm});
            skLineSegment(sketch, "E335.MirrorCS", {"start": v(-9.71, 16.83) * mm, "end": v(-12.21, 16.83) * mm});
            skLineSegment(sketch, "E336.MirrorCS", {"start": v(-12.21, 16.83) * mm, "end": v(-13.46, 19) * mm});
            skLineSegment(sketch, "E337.MirrorCS", {"start": v(-13.46, 19) * mm, "end": v(-12.21, 21.16) * mm});
            skLineSegment(sketch, "E338.MirrorCS", {"start": v(-12.21, 21.16) * mm, "end": v(-9.71, 21.16) * mm});
            skLineSegment(sketch, "E339.MirrorCS", {"start": v(-9.71, 21.16) * mm, "end": v(-8.46, 19) * mm});
            skLineSegment(sketch, "E340.MirrorCS", {"start": v(9.14, 22.16) * mm, "end": v(7.3, 19) * mm});
            skLineSegment(sketch, "E341.MirrorCS", {"start": v(12.8, 22.16) * mm, "end": v(9.14, 22.16) * mm});
            skLineSegment(sketch, "E342.MirrorCS", {"start": v(14.62, 19) * mm, "end": v(12.8, 22.16) * mm});
            skLineSegment(sketch, "E343.MirrorCS", {"start": v(12.21, 16.83) * mm, "end": v(13.46, 19) * mm});
            skLineSegment(sketch, "E344.MirrorCS", {"start": v(12.8, 15.83) * mm, "end": v(14.62, 19) * mm});
            skLineSegment(sketch, "E345.MirrorCS", {"start": v(9.71, 16.83) * mm, "end": v(12.21, 16.83) * mm});
            skLineSegment(sketch, "E346.MirrorCS", {"start": v(9.71, 16.83) * mm, "end": v(8.46, 19) * mm});
            skLineSegment(sketch, "E347.MirrorCS", {"start": v(9.71, 21.16) * mm, "end": v(8.46, 19) * mm});
            skLineSegment(sketch, "E348.MirrorCS", {"start": v(12.21, 21.16) * mm, "end": v(9.71, 21.16) * mm});
            skLineSegment(sketch, "E349.MirrorCS", {"start": v(13.46, 19) * mm, "end": v(12.21, 21.16) * mm});
            skLineSegment(sketch, "E350.MirrorCS", {"start": v(-1.83, -15.83) * mm, "end": v(-3.65, -19) * mm});
            skLineSegment(sketch, "E351.MirrorCS", {"start": v(1.83, -15.83) * mm, "end": v(3.65, -19) * mm});
            skLineSegment(sketch, "E352.MirrorCS", {"start": v(1.83, -22.16) * mm, "end": v(3.65, -19) * mm});
            skLineSegment(sketch, "E353.MirrorCS", {"start": v(-1.83, -22.16) * mm, "end": v(1.83, -22.16) * mm});
            skLineSegment(sketch, "E354.MirrorCS", {"start": v(-1.83, -22.16) * mm, "end": v(-3.65, -19) * mm});
            skLineSegment(sketch, "E355.MirrorCS", {"start": v(-2.5, -19) * mm, "end": v(-1.25, -16.83) * mm});
            skLineSegment(sketch, "E356.MirrorCS", {"start": v(-1.25, -16.83) * mm, "end": v(1.25, -16.83) * mm});
            skLineSegment(sketch, "E357.MirrorCS", {"start": v(1.25, -16.83) * mm, "end": v(2.5, -19) * mm});
            skLineSegment(sketch, "E358.MirrorCS", {"start": v(1.25, -21.16) * mm, "end": v(2.5, -19) * mm});
            skLineSegment(sketch, "E359.MirrorCS", {"start": v(1.25, -21.16) * mm, "end": v(-1.25, -21.16) * mm});
            skLineSegment(sketch, "E360.MirrorCS", {"start": v(-1.25, -21.16) * mm, "end": v(-2.5, -19) * mm});
            skLineSegment(sketch, "E361.MirrorCS", {"start": v(7.3, -19) * mm, "end": v(3.65, -19) * mm});
            skLineSegment(sketch, "E362.MirrorCS", {"start": v(9.14, -15.83) * mm, "end": v(7.3, -19) * mm});
            skLineSegment(sketch, "E363.MirrorCS", {"start": v(9.71, -14.83) * mm, "end": v(8.46, -12.66) * mm});
            skLineSegment(sketch, "E364.MirrorCS", {"start": v(9.14, -15.83) * mm, "end": v(7.3, -12.66) * mm});
            skLineSegment(sketch, "E365.MirrorCS", {"start": v(7.98, -15.83) * mm, "end": v(6.73, -13.66) * mm});
            skLineSegment(sketch, "E366.MirrorCS", {"start": v(4.23, -13.66) * mm, "end": v(6.73, -13.66) * mm});
            skLineSegment(sketch, "E367.MirrorCS", {"start": v(2.98, -15.83) * mm, "end": v(4.23, -13.66) * mm});
            skLineSegment(sketch, "E368.MirrorCS", {"start": v(4.23, -18) * mm, "end": v(2.98, -15.83) * mm});
            skLineSegment(sketch, "E369.MirrorCS", {"start": v(6.73, -18) * mm, "end": v(4.23, -18) * mm});
            skLineSegment(sketch, "E370.MirrorCS", {"start": v(7.98, -15.83) * mm, "end": v(6.73, -18) * mm});
            skLineSegment(sketch, "E371.MirrorCS", {"start": v(-9.14, -15.83) * mm, "end": v(-7.3, -12.66) * mm});
            skLineSegment(sketch, "E372.MirrorCS", {"start": v(-9.14, -15.83) * mm, "end": v(-7.3, -19) * mm});
            skLineSegment(sketch, "E373.MirrorCS", {"start": v(-7.3, -19) * mm, "end": v(-3.65, -19) * mm});
            skLineSegment(sketch, "E374.MirrorCS", {"start": v(-4.23, -18) * mm, "end": v(-2.98, -15.83) * mm});
            skLineSegment(sketch, "E375.MirrorCS", {"start": v(-2.98, -15.83) * mm, "end": v(-4.23, -13.66) * mm});
            skLineSegment(sketch, "E376.MirrorCS", {"start": v(-4.23, -13.66) * mm, "end": v(-6.73, -13.66) * mm});
            skLineSegment(sketch, "E377.MirrorCS", {"start": v(-7.98, -15.83) * mm, "end": v(-6.73, -13.66) * mm});
            skLineSegment(sketch, "E378.MirrorCS", {"start": v(-7.98, -15.83) * mm, "end": v(-6.73, -18) * mm});
            skLineSegment(sketch, "E379.MirrorCS", {"start": v(-6.73, -18) * mm, "end": v(-4.23, -18) * mm});
            skLineSegment(sketch, "E380.MirrorCS", {"start": v(-12.8, -15.83) * mm, "end": v(-14.62, -12.66) * mm});
            skLineSegment(sketch, "E381.MirrorCS", {"start": v(-9.14, -15.83) * mm, "end": v(-12.8, -15.83) * mm});
            skLineSegment(sketch, "E382.MirrorCS", {"start": v(-9.71, -14.83) * mm, "end": v(-8.46, -12.66) * mm});
            skLineSegment(sketch, "E383.MirrorCS", {"start": v(-9.71, -10.5) * mm, "end": v(-8.46, -12.66) * mm});
            skLineSegment(sketch, "E384.MirrorCS", {"start": v(-12.21, -10.5) * mm, "end": v(-9.71, -10.5) * mm});
            skLineSegment(sketch, "E385.MirrorCS", {"start": v(-13.46, -12.66) * mm, "end": v(-12.21, -10.5) * mm});
            skLineSegment(sketch, "E386.MirrorCS", {"start": v(-12.21, -14.83) * mm, "end": v(-13.46, -12.66) * mm});
            skLineSegment(sketch, "E387.MirrorCS", {"start": v(-9.71, -14.83) * mm, "end": v(-12.21, -14.83) * mm});
            skLineSegment(sketch, "E388.MirrorCS", {"start": v(-9.71, -16.83) * mm, "end": v(-12.21, -16.83) * mm});
            skLineSegment(sketch, "E389.MirrorCS", {"start": v(-9.71, -16.83) * mm, "end": v(-8.46, -19) * mm});
            skLineSegment(sketch, "E390.MirrorCS", {"start": v(-9.71, -21.16) * mm, "end": v(-8.46, -19) * mm});
            skLineSegment(sketch, "E391.MirrorCS", {"start": v(-12.21, -21.16) * mm, "end": v(-9.71, -21.16) * mm});
            skLineSegment(sketch, "E392.MirrorCS", {"start": v(-13.46, -19) * mm, "end": v(-12.21, -21.16) * mm});
            skLineSegment(sketch, "E393.MirrorCS", {"start": v(-12.21, -16.83) * mm, "end": v(-13.46, -19) * mm});
            skLineSegment(sketch, "E394.MirrorCS", {"start": v(-12.8, -15.83) * mm, "end": v(-14.62, -19) * mm});
            skLineSegment(sketch, "E395.MirrorCS", {"start": v(-9.14, -22.16) * mm, "end": v(-7.3, -19) * mm});
            skLineSegment(sketch, "E396.MirrorCS", {"start": v(-14.62, -19) * mm, "end": v(-12.8, -22.16) * mm});
            skLineSegment(sketch, "E397.MirrorCS", {"start": v(-12.8, -22.16) * mm, "end": v(-9.14, -22.16) * mm});
            skLineSegment(sketch, "E398.MirrorCS", {"start": v(12.21, -10.5) * mm, "end": v(9.71, -10.5) * mm});
            skLineSegment(sketch, "E399.MirrorCS", {"start": v(13.46, -12.66) * mm, "end": v(12.21, -10.5) * mm});
            skLineSegment(sketch, "E400.MirrorCS", {"start": v(9.71, -10.5) * mm, "end": v(8.46, -12.66) * mm});
            skLineSegment(sketch, "E401.MirrorCS", {"start": v(9.71, -14.83) * mm, "end": v(12.21, -14.83) * mm});
            skLineSegment(sketch, "E402.MirrorCS", {"start": v(12.21, -14.83) * mm, "end": v(13.46, -12.66) * mm});
            skLineSegment(sketch, "E403.MirrorCS", {"start": v(9.14, -15.83) * mm, "end": v(12.8, -15.83) * mm});
            skLineSegment(sketch, "E404.MirrorCS", {"start": v(12.8, -15.83) * mm, "end": v(14.62, -12.66) * mm});
            skLineSegment(sketch, "E405.MirrorCS", {"start": v(14.62, -12.66) * mm, "end": v(12.8, -9.5) * mm});
            skLineSegment(sketch, "E406.MirrorCS", {"start": v(9.14, -22.16) * mm, "end": v(7.3, -19) * mm});
            skLineSegment(sketch, "E407.MirrorCS", {"start": v(12.8, -22.16) * mm, "end": v(9.14, -22.16) * mm});
            skLineSegment(sketch, "E408.MirrorCS", {"start": v(14.62, -19) * mm, "end": v(12.8, -22.16) * mm});
            skLineSegment(sketch, "E409.MirrorCS", {"start": v(12.8, -15.83) * mm, "end": v(14.62, -19) * mm});
            skLineSegment(sketch, "E410.MirrorCS", {"start": v(12.21, -16.83) * mm, "end": v(13.46, -19) * mm});
            skLineSegment(sketch, "E411.MirrorCS", {"start": v(13.46, -19) * mm, "end": v(12.21, -21.16) * mm});
            skLineSegment(sketch, "E412.MirrorCS", {"start": v(12.21, -21.16) * mm, "end": v(9.71, -21.16) * mm});
            skLineSegment(sketch, "E413.MirrorCS", {"start": v(9.71, -21.16) * mm, "end": v(8.46, -19) * mm});
            skLineSegment(sketch, "E414.MirrorCS", {"start": v(9.71, -16.83) * mm, "end": v(8.46, -19) * mm});
            skLineSegment(sketch, "E415.MirrorCS", {"start": v(9.71, -16.83) * mm, "end": v(12.21, -16.83) * mm});
            skSolve(sketch);
        }
        {
            var Q0;
            {var subQ0=sQuery(id+"F2.wireOp",EDGE,"E381.MirrorCS");var subQ1=sQuery(id+"F2.wireOp",EDGE,"E10.0");var subQ2=makeQuery(id+"F2.imprint","INTERSECT",VERTEX,{"derivedFrom":[subQ1,subQ0]});Q0=makeQuery(id+"F2.imprint","IMPRINT",FACE,{"disambiguationData":[TD([[makeQuery(id+"F2.imprint","IMPRINT",EDGE,{"disambiguationData":[TD([[subQ2,-1.0]])],"derivedFrom":subQ1}),1.0]])]});}
            var Q1;
            Q1=makeQuery(id+"F2.imprint","IMPRINT",FACE,{"disambiguationData":[TD([[makeQuery(id+"F2.imprint","IMPRINT",EDGE,{"derivedFrom":sQuery(id+"F2.wireOp",EDGE,"E87.MirrorCS")}),-1.0]])]});
            var Q2;
            Q2=makeQuery(id+"F2.imprint","IMPRINT",FACE,{"disambiguationData":[TD([[makeQuery(id+"F2.imprint","IMPRINT",EDGE,{"derivedFrom":sQuery(id+"F2.wireOp",EDGE,"E86.MirrorCS")}),-1.0]])]});
            var Q3;
            Q3=makeQuery(id+"F2.imprint","IMPRINT",FACE,{"disambiguationData":[TD([[makeQuery(id+"F2.imprint","IMPRINT",EDGE,{"derivedFrom":sQuery(id+"F2.wireOp",EDGE,"E36.MirrorCS")}),1.0]])]});
            var Q4;
            Q4=makeQuery(id+"F2.imprint","IMPRINT",FACE,{"disambiguationData":[TD([[makeQuery(id+"F2.imprint","IMPRINT",EDGE,{"derivedFrom":sQuery(id+"F2.wireOp",EDGE,"E77.MirrorCS")}),1.0]])]});
            var Q5;
            Q5=makeQuery(id+"F2.imprint","IMPRINT",FACE,{"disambiguationData":[TD([[makeQuery(id+"F2.imprint","IMPRINT",EDGE,{"derivedFrom":sQuery(id+"F2.wireOp",EDGE,"E37.MirrorCS")}),-1.0]])]});
            var Q6;
            Q6=makeQuery(id+"F2.imprint","IMPRINT",FACE,{"disambiguationData":[TD([[makeQuery(id+"F2.imprint","IMPRINT",EDGE,{"derivedFrom":sQuery(id+"F2.wireOp",EDGE,"E76.MirrorCS")}),-1.0]])]});
            var Q7;
            Q7=makeQuery(id+"F2.imprint","IMPRINT",FACE,{"disambiguationData":[TD([[makeQuery(id+"F2.imprint","IMPRINT",EDGE,{"derivedFrom":sQuery(id+"F2.wireOp",EDGE,"E26.3")}),-1.0]])]});
            var Q8;
            {var subQ4=sQuery(id+"F2.wireOp",EDGE,"E33.MirrorCS");Q8=makeQuery(id+"F2.imprint","IMPRINT",FACE,{"disambiguationData":[TD([[makeQuery(id+"F2.imprint","IMPRINT",EDGE,{"derivedFrom":subQ4}),-1.0]])]});}
            var Q9;
            Q9=makeQuery(id+"F2.imprint","IMPRINT",FACE,{"disambiguationData":[TD([[makeQuery(id+"F2.imprint","IMPRINT",EDGE,{"derivedFrom":sQuery(id+"F2.wireOp",EDGE,"E35.MirrorCS")}),1.0]])]});
            var Q10;
            {var subQ1=sQuery(id+"F2.wireOp",EDGE,"E193.MirrorCS");Q10=makeQuery(id+"F2.imprint","IMPRINT",FACE,{"disambiguationData":[TD([[makeQuery(id+"F2.imprint","IMPRINT",EDGE,{"derivedFrom":subQ1}),-1.0]])]});}
            var Q11;
            Q11=makeQuery(id+"F2.imprint","IMPRINT",FACE,{"disambiguationData":[TD([[makeQuery(id+"F2.imprint","IMPRINT",EDGE,{"derivedFrom":sQuery(id+"F2.wireOp",EDGE,"E90.MirrorCS")}),1.0]])]});
            var Q12;
            Q12=makeQuery(id+"F2.imprint","IMPRINT",FACE,{"disambiguationData":[TD([[makeQuery(id+"F2.imprint","IMPRINT",EDGE,{"derivedFrom":sQuery(id+"F2.wireOp",EDGE,"E91.MirrorCS")}),1.0]])]});
            var Q13;
            {var subQ0=sQuery(id+"F2.wireOp",EDGE,"E362.MirrorCS");var subQ1=sQuery(id+"F2.wireOp",EDGE,"E10.0");var subQ2=makeQuery(id+"F2.imprint","INTERSECT",VERTEX,{"derivedFrom":[subQ1,subQ0]});Q13=makeQuery(id+"F2.imprint","IMPRINT",FACE,{"disambiguationData":[TD([[makeQuery(id+"F2.imprint","IMPRINT",EDGE,{"disambiguationData":[TD([[subQ2,-1.0]])],"derivedFrom":subQ1}),1.0]])]});}
            var Q14;
            Q14=makeQuery(id+"F2.imprint","IMPRINT",FACE,{"disambiguationData":[TD([[makeQuery(id+"F2.imprint","IMPRINT",EDGE,{"derivedFrom":sQuery(id+"F2.wireOp",EDGE,"E131.MirrorCS")}),1.0]])]});
            var Q15;
            {var subQ5=sQuery(id+"F2.wireOp",EDGE,"E138.MirrorCS");Q15=makeQuery(id+"F2.imprint","IMPRINT",FACE,{"disambiguationData":[TD([[makeQuery(id+"F2.imprint","IMPRINT",EDGE,{"derivedFrom":subQ5}),-1.0]])]});}
            var Q16;
            Q16=makeQuery(id+"F2.imprint","IMPRINT",FACE,{"disambiguationData":[TD([[makeQuery(id+"F2.imprint","IMPRINT",EDGE,{"derivedFrom":sQuery(id+"F2.wireOp",EDGE,"E133.MirrorCS")}),1.0]])]});
            var Q17;
            Q17=makeQuery(id+"F2.imprint","IMPRINT",FACE,{"disambiguationData":[TD([[makeQuery(id+"F2.imprint","IMPRINT",EDGE,{"derivedFrom":sQuery(id+"F2.wireOp",EDGE,"E134.MirrorCS")}),1.0]])]});
            var Q18;
            {var subQ1=sQuery(id+"F2.wireOp",EDGE,"E217.MirrorCS");var subQ3=sQuery(id+"F2.wireOp",EDGE,"E10.0");var subQ4=makeQuery(id+"F2.imprint","INTERSECT",VERTEX,{"derivedFrom":[subQ1,subQ3]});Q18=makeQuery(id+"F2.imprint","IMPRINT",FACE,{"disambiguationData":[TD([[makeQuery(id+"F2.imprint","IMPRINT",EDGE,{"disambiguationData":[TD([[subQ4,-1.0]])],"derivedFrom":subQ3}),1.0]])]});}
            var Q19;
            {var subQ4=sQuery(id+"F2.wireOp",EDGE,"E136.MirrorCS");Q19=makeQuery(id+"F2.imprint","IMPRINT",FACE,{"disambiguationData":[TD([[makeQuery(id+"F2.imprint","IMPRINT",EDGE,{"derivedFrom":subQ4}),-1.0]])]});}
            var Q20;
            Q20=makeQuery(id+"F2.imprint","IMPRINT",FACE,{"disambiguationData":[TD([[makeQuery(id+"F2.imprint","IMPRINT",EDGE,{"derivedFrom":sQuery(id+"F2.wireOp",EDGE,"E104.MirrorCS")}),1.0]])]});
            var Q21;
            Q21=makeQuery(id+"F2.imprint","IMPRINT",FACE,{"disambiguationData":[TD([[makeQuery(id+"F2.imprint","IMPRINT",EDGE,{"derivedFrom":sQuery(id+"F2.wireOp",EDGE,"E101.MirrorCS")}),-1.0]])]});
            var Q22;
            Q22=makeQuery(id+"F2.imprint","IMPRINT",FACE,{"disambiguationData":[TD([[makeQuery(id+"F2.imprint","IMPRINT",EDGE,{"derivedFrom":sQuery(id+"F2.wireOp",EDGE,"E293.MirrorCS")}),-1.0]])]});
            var Q23;
            {var subQ0=sQuery(id+"F2.wireOp",EDGE,"E303.MirrorCS");var subQ1=sQuery(id+"F2.wireOp",EDGE,"E10.0");var subQ2=makeQuery(id+"F2.imprint","INTERSECT",VERTEX,{"derivedFrom":[subQ1,subQ0]});Q23=makeQuery(id+"F2.imprint","IMPRINT",FACE,{"disambiguationData":[TD([[makeQuery(id+"F2.imprint","IMPRINT",EDGE,{"disambiguationData":[TD([[subQ2,-1.0]])],"derivedFrom":subQ1}),1.0]])]});}
            var Q24;
            {var subQ9=sQuery(id+"F2.wireOp",EDGE,"E202.MirrorCS");Q24=makeQuery(id+"F2.imprint","IMPRINT",FACE,{"disambiguationData":[TD([[makeQuery(id+"F2.imprint","IMPRINT",EDGE,{"derivedFrom":subQ9}),1.0]])]});}
            var Q25;
            Q25=makeQuery(id+"F2.imprint","IMPRINT",FACE,{"disambiguationData":[TD([[makeQuery(id+"F2.imprint","IMPRINT",EDGE,{"derivedFrom":sQuery(id+"F2.wireOp",EDGE,"E45.MirrorCS")}),1.0]])]});
            var Q26;
            Q26=makeQuery(id+"F2.imprint","IMPRINT",FACE,{"disambiguationData":[TD([[makeQuery(id+"F2.imprint","IMPRINT",EDGE,{"derivedFrom":sQuery(id+"F2.wireOp",EDGE,"E312.MirrorCS")}),1.0]])]});
            var Q27;
            Q27=makeQuery(id+"F2.imprint","IMPRINT",FACE,{"disambiguationData":[TD([[makeQuery(id+"F2.imprint","IMPRINT",EDGE,{"derivedFrom":sQuery(id+"F2.wireOp",EDGE,"E47.MirrorCS")}),-1.0]])]});
            var Q28;
            Q28=makeQuery(id+"F2.imprint","IMPRINT",FACE,{"disambiguationData":[TD([[makeQuery(id+"F2.imprint","IMPRINT",EDGE,{"derivedFrom":sQuery(id+"F2.wireOp",EDGE,"E39.MirrorCS")}),-1.0]])]});
            var Q29;
            {var subQ5=sQuery(id+"F2.wireOp",EDGE,"E159.MirrorCS");Q29=makeQuery(id+"F2.imprint","IMPRINT",FACE,{"disambiguationData":[TD([[makeQuery(id+"F2.imprint","IMPRINT",EDGE,{"derivedFrom":subQ5}),-1.0]])]});}
            var Q30;
            Q30=makeQuery(id+"F2.imprint","IMPRINT",FACE,{"disambiguationData":[TD([[makeQuery(id+"F2.imprint","IMPRINT",EDGE,{"derivedFrom":sQuery(id+"F2.wireOp",EDGE,"E162.MirrorCS")}),-1.0]])]});
            var Q31;
            {var subQ1=sQuery(id+"F2.wireOp",EDGE,"E165.MirrorCS");Q31=makeQuery(id+"F2.imprint","IMPRINT",FACE,{"disambiguationData":[TD([[makeQuery(id+"F2.imprint","IMPRINT",EDGE,{"derivedFrom":subQ1}),1.0]])]});}
            var Q32;
            {var subQ1=sQuery(id+"F2.wireOp",EDGE,"E248.MirrorCS");var subQ3=sQuery(id+"F2.wireOp",EDGE,"E10.0");var subQ4=makeQuery(id+"F2.imprint","INTERSECT",VERTEX,{"derivedFrom":[subQ1,subQ3]});Q32=makeQuery(id+"F2.imprint","IMPRINT",FACE,{"disambiguationData":[TD([[makeQuery(id+"F2.imprint","IMPRINT",EDGE,{"disambiguationData":[TD([[subQ4,1.0]])],"derivedFrom":subQ3}),1.0]])]});}
            var Q33;
            {var subQ5=sQuery(id+"F2.wireOp",EDGE,"E158.MirrorCS");Q33=makeQuery(id+"F2.imprint","IMPRINT",FACE,{"disambiguationData":[TD([[makeQuery(id+"F2.imprint","IMPRINT",EDGE,{"derivedFrom":subQ5}),1.0]])]});}
            var Q34;
            {var subQ13=sQuery(id+"F2.wireOp",EDGE,"E75.MirrorCS");Q34=makeQuery(id+"F2.imprint","IMPRINT",FACE,{"disambiguationData":[TD([[makeQuery(id+"F2.imprint","IMPRINT",EDGE,{"derivedFrom":subQ13}),1.0]])]});}
            var Q35;
            {var subQ0=sQuery(id+"F2.wireOp",EDGE,"E96.MirrorCS");var subQ3=sQuery(id+"F2.wireOp",EDGE,"E14");var subQ7=makeQuery(id+"F2.imprint","INTERSECT",VERTEX,{"derivedFrom":[subQ3,subQ0]});Q35=makeQuery(id+"F2.imprint","IMPRINT",FACE,{"disambiguationData":[TD([[makeQuery(id+"F2.imprint","IMPRINT",EDGE,{"disambiguationData":[TD([[subQ7,-1.0]])],"derivedFrom":subQ3}),-1.0]])]});}
            var Q36;
            {var subQ0=sQuery(id+"F2.wireOp",EDGE,"E34.MirrorCS");var subQ3=sQuery(id+"F2.wireOp",EDGE,"E15");var subQ4=makeQuery(id+"F2.imprint","INTERSECT",VERTEX,{"derivedFrom":[subQ3,subQ0]});Q36=makeQuery(id+"F2.imprint","IMPRINT",FACE,{"disambiguationData":[TD([[makeQuery(id+"F2.imprint","IMPRINT",EDGE,{"disambiguationData":[TD([[subQ4,-1.0]])],"derivedFrom":subQ3}),1.0]])]});}
            var Q37;
            {var subQ0=sQuery(id+"F2.wireOp",EDGE,"E96.MirrorCS");var subQ1=sQuery(id+"F2.wireOp",EDGE,"E14");var subQ2=makeQuery(id+"F2.imprint","INTERSECT",VERTEX,{"derivedFrom":[subQ1,subQ0]});Q37=makeQuery(id+"F2.imprint","IMPRINT",FACE,{"disambiguationData":[TD([[makeQuery(id+"F2.imprint","IMPRINT",EDGE,{"disambiguationData":[TD([[subQ2,-1.0]])],"derivedFrom":subQ1}),1.0]])]});}
            var Q38;
            Q38=makeQuery(id+"F2.imprint","IMPRINT",FACE,{"disambiguationData":[TD([[makeQuery(id+"F2.imprint","IMPRINT",EDGE,{"derivedFrom":sQuery(id+"F2.wireOp",EDGE,"E99.MirrorCS")}),1.0]])]});
            var Q39;
            Q39=makeQuery(id+"F2.imprint","IMPRINT",FACE,{"disambiguationData":[TD([[makeQuery(id+"F2.imprint","IMPRINT",EDGE,{"derivedFrom":sQuery(id+"F2.wireOp",EDGE,"E130.MirrorCS")}),-1.0]])]});
            var Q40;
            {var subQ1=sQuery(id+"F2.wireOp",EDGE,"E26.2");var subQ3=sQuery(id+"F2.wireOp",EDGE,"E14");var subQ5=makeQuery(id+"F2.imprint","INTERSECT",VERTEX,{"derivedFrom":[subQ3,subQ1]});Q40=makeQuery(id+"F2.imprint","IMPRINT",FACE,{"disambiguationData":[TD([[makeQuery(id+"F2.imprint","IMPRINT",EDGE,{"disambiguationData":[TD([[subQ5,-1.0]])],"derivedFrom":subQ3}),-1.0]])]});}
            var Q41;
            {var subQ0=sQuery(id+"F2.wireOp",EDGE,"E114.MirrorCS");var subQ1=sQuery(id+"F2.wireOp",EDGE,"E14");var subQ2=makeQuery(id+"F2.imprint","INTERSECT",VERTEX,{"derivedFrom":[subQ1,subQ0]});Q41=makeQuery(id+"F2.imprint","IMPRINT",FACE,{"disambiguationData":[TD([[makeQuery(id+"F2.imprint","IMPRINT",EDGE,{"disambiguationData":[TD([[subQ2,-1.0]])],"derivedFrom":subQ1}),1.0]])]});}
            var Q42;
            {var subQ1=sQuery(id+"F2.wireOp",EDGE,"E15");var subQ4=sQuery(id+"F2.wireOp",EDGE,"E26.0");var subQ5=makeQuery(id+"F2.imprint","INTERSECT",VERTEX,{"derivedFrom":[subQ1,subQ4]});Q42=makeQuery(id+"F2.imprint","IMPRINT",FACE,{"disambiguationData":[TD([[makeQuery(id+"F2.imprint","IMPRINT",EDGE,{"disambiguationData":[TD([[subQ5,1.0]])],"derivedFrom":subQ4}),1.0]])]});}
            var Q43;
            {var subQ1=sQuery(id+"F2.wireOp",EDGE,"E14");var subQ4=sQuery(id+"F2.wireOp",EDGE,"E26.1");var subQ5=makeQuery(id+"F2.imprint","INTERSECT",VERTEX,{"derivedFrom":[subQ1,subQ4]});Q43=makeQuery(id+"F2.imprint","IMPRINT",FACE,{"disambiguationData":[TD([[makeQuery(id+"F2.imprint","IMPRINT",EDGE,{"disambiguationData":[TD([[subQ5,-1.0]])],"derivedFrom":subQ4}),1.0]])]});}
            var Q44;
            {var subQ10=sQuery(id+"F2.wireOp",EDGE,"E26.3");Q44=makeQuery(id+"F2.imprint","IMPRINT",FACE,{"disambiguationData":[TD([[makeQuery(id+"F2.imprint","IMPRINT",EDGE,{"derivedFrom":subQ10}),1.0]])]});}
            var Q45;
            {var subQ11=sQuery(id+"F2.wireOp",EDGE,"E26.4");Q45=makeQuery(id+"F2.imprint","IMPRINT",FACE,{"disambiguationData":[TD([[makeQuery(id+"F2.imprint","IMPRINT",EDGE,{"derivedFrom":subQ11}),1.0]])]});}
            var Q46;
            {var subQ0=sQuery(id+"F2.wireOp",EDGE,"E13");var subQ1=sQuery(id+"F2.wireOp",EDGE,"E11");var subQ2=makeQuery(id+"F2.imprint","INTERSECT",VERTEX,{"disambiguationData":[OD(0.0)],"derivedFrom":[subQ1,subQ0]});Q46=makeQuery(id+"F2.imprint","IMPRINT",FACE,{"disambiguationData":[TD([[makeQuery(id+"F2.imprint","IMPRINT",EDGE,{"disambiguationData":[TD([[subQ2,-1.0]])],"derivedFrom":subQ0}),-1.0]])]});}
            var Q47;
            {var subQ0=sQuery(id+"F2.wireOp",EDGE,"E13");var subQ1=sQuery(id+"F2.wireOp",EDGE,"E11");var subQ2=makeQuery(id+"F2.imprint","INTERSECT",VERTEX,{"disambiguationData":[OD(0.0)],"derivedFrom":[subQ1,subQ0]});Q47=makeQuery(id+"F2.imprint","IMPRINT",FACE,{"disambiguationData":[TD([[makeQuery(id+"F2.imprint","IMPRINT",EDGE,{"disambiguationData":[TD([[subQ2,-1.0]])],"derivedFrom":subQ0}),1.0]])]});}
            var Q48;
            {var subQ0=sQuery(id+"F2.wireOp",EDGE,"E21");Q48=makeQuery(id+"F2.imprint","IMPRINT",FACE,{"disambiguationData":[TD([[makeQuery(id+"F2.imprint","IMPRINT",EDGE,{"derivedFrom":subQ0}),1.0]])]});}
            var Q49;
            {var subQ0=sQuery(id+"F2.wireOp",EDGE,"E20");Q49=makeQuery(id+"F2.imprint","IMPRINT",FACE,{"disambiguationData":[TD([[makeQuery(id+"F2.imprint","IMPRINT",EDGE,{"derivedFrom":subQ0}),-1.0]])]});}
            var Q50;
            {var subQ0=sQuery(id+"F2.wireOp",EDGE,"E13");var subQ1=sQuery(id+"F2.wireOp",EDGE,"E11");var subQ2=makeQuery(id+"F2.imprint","INTERSECT",VERTEX,{"disambiguationData":[OD(1.0)],"derivedFrom":[subQ1,subQ0]});Q50=makeQuery(id+"F2.imprint","IMPRINT",FACE,{"disambiguationData":[TD([[makeQuery(id+"F2.imprint","IMPRINT",EDGE,{"disambiguationData":[TD([[subQ2,1.0]])],"derivedFrom":subQ0}),-1.0]])]});}
            var Q51;
            {var subQ0=sQuery(id+"F2.wireOp",EDGE,"E13");var subQ1=sQuery(id+"F2.wireOp",EDGE,"E11");var subQ2=makeQuery(id+"F2.imprint","INTERSECT",VERTEX,{"disambiguationData":[OD(1.0)],"derivedFrom":[subQ1,subQ0]});Q51=makeQuery(id+"F2.imprint","IMPRINT",FACE,{"disambiguationData":[TD([[makeQuery(id+"F2.imprint","IMPRINT",EDGE,{"disambiguationData":[TD([[subQ2,1.0]])],"derivedFrom":subQ0}),1.0]])]});}
            var Q52;
            {var subQ0=sQuery(id+"F2.wireOp",EDGE,"E24");Q52=makeQuery(id+"F2.imprint","IMPRINT",FACE,{"disambiguationData":[TD([[makeQuery(id+"F2.imprint","IMPRINT",EDGE,{"derivedFrom":subQ0}),-1.0]])]});}
            var Q53;
            {var subQ0=sQuery(id+"F2.wireOp",EDGE,"E23");Q53=makeQuery(id+"F2.imprint","IMPRINT",FACE,{"disambiguationData":[TD([[makeQuery(id+"F2.imprint","IMPRINT",EDGE,{"derivedFrom":subQ0}),-1.0]])]});}
            var Q54;
            Q54=makeQuery(id+"F2.imprint","IMPRINT",FACE,{"disambiguationData":[TD([[makeQuery(id+"F2.imprint","IMPRINT",EDGE,{"derivedFrom":sQuery(id+"F2.wireOp",EDGE,"E26.4")}),-1.0]])]});
            var Q55;
            Q55=makeQuery(id+"F2.imprint","IMPRINT",FACE,{"disambiguationData":[TD([[makeQuery(id+"F2.imprint","IMPRINT",EDGE,{"derivedFrom":sQuery(id+"F2.wireOp",EDGE,"E56.MirrorCS")}),1.0]])]});
            var Q56;
            {var subQ5=sQuery(id+"F2.wireOp",EDGE,"E62.MirrorCS");Q56=makeQuery(id+"F2.imprint","IMPRINT",FACE,{"disambiguationData":[TD([[makeQuery(id+"F2.imprint","IMPRINT",EDGE,{"derivedFrom":subQ5}),1.0]])]});}
            var Q57;
            {var subQ1=sQuery(id+"F2.wireOp",EDGE,"E26.5");var subQ3=sQuery(id+"F2.wireOp",EDGE,"E15");var subQ4=makeQuery(id+"F2.imprint","INTERSECT",VERTEX,{"derivedFrom":[subQ3,subQ1]});Q57=makeQuery(id+"F2.imprint","IMPRINT",FACE,{"disambiguationData":[TD([[makeQuery(id+"F2.imprint","IMPRINT",EDGE,{"disambiguationData":[TD([[subQ4,-1.0]])],"derivedFrom":subQ3}),1.0]])]});}
            var Q58;
            Q58=makeQuery(id+"F2.imprint","IMPRINT",FACE,{"disambiguationData":[TD([[makeQuery(id+"F2.imprint","IMPRINT",EDGE,{"derivedFrom":sQuery(id+"F2.wireOp",EDGE,"E39.MirrorCS")}),1.0]])]});
            var Q59;
            {var subQ0=sQuery(id+"F2.wireOp",EDGE,"E314.MirrorCS");var subQ1=sQuery(id+"F2.wireOp",EDGE,"E10.0");var subQ2=makeQuery(id+"F2.imprint","INTERSECT",VERTEX,{"derivedFrom":[subQ1,subQ0]});Q59=makeQuery(id+"F2.imprint","IMPRINT",FACE,{"disambiguationData":[TD([[makeQuery(id+"F2.imprint","IMPRINT",EDGE,{"disambiguationData":[TD([[subQ2,-1.0]])],"derivedFrom":subQ1}),1.0]])]});}
            extrude(context, id + "F3", {"entities" : qUnion([Q0, Q1, Q2, Q3, Q4, Q5, Q6, Q7, Q8, Q9, Q10, Q11, Q12, Q13, Q14, Q15, Q16, Q17, Q18, Q19, Q20, Q21, Q22, Q23, Q24, Q25, Q26, Q27, Q28, Q29, Q30, Q31, Q32, Q33, Q34, Q35, Q36, Q37, Q38, Q39, Q40, Q41, Q42, Q43, Q44, Q45, Q46, Q47, Q48, Q49, Q50, Q51, Q52, Q53, Q54, Q55, Q56, Q57, Q58, Q59]), "operationType" : NewBodyOperationType.ADD, "oppositeDirection" : true, "depth" : 3 * mm, "offsetDistance" : 25 * mm});
        }
    });
